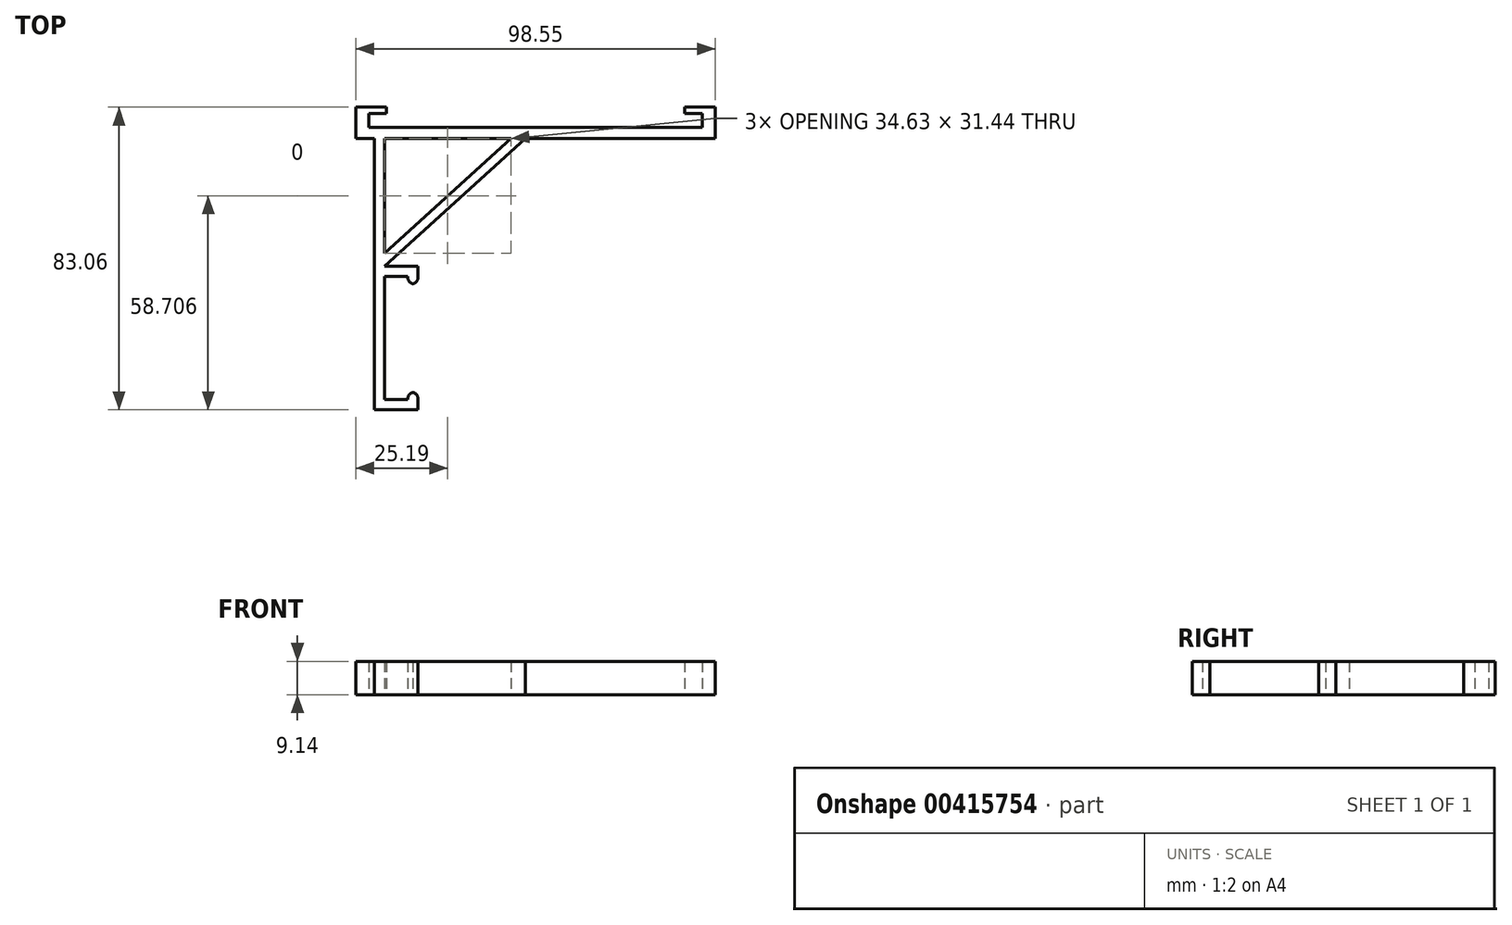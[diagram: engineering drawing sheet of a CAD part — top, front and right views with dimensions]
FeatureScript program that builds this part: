
annotation { "Feature Type Name" : "Feature", "Feature Type Description" : "" }
export const myFeature = defineFeature(function(context is Context, id is Id, definition is map)
    precondition{}
    {
        {
            var Q0;
            Q0=qCreatedBy(makeId("Top.planeOp"),FACE);
            var sketch = newSketch(context, id + "F0", { "sketchPlane" : qUnion([Q0])});
            skLineSegment(sketch, "E0", {"start": v(-45.89, 21.6) * mm, "end": v(-54.27, 21.6) * mm});
            skLineSegment(sketch, "E1", {"start": v(-54.27, 21.6) * mm, "end": v(-54.27, 12.96) * mm});
            skLineSegment(sketch, "E2", {"start": v(-54.27, 12.96) * mm, "end": v(-49.19, 12.96) * mm});
            skLineSegment(sketch, "E3", {"start": v(44.28, 12.96) * mm, "end": v(44.28, 21.6) * mm});
            skLineSegment(sketch, "E4", {"start": v(44.28, 21.6) * mm, "end": v(35.9, 21.6) * mm});
            skLineSegment(sketch, "E5", {"start": v(35.9, 21.6) * mm, "end": v(35.9, 19.81) * mm});
            skLineSegment(sketch, "E6", {"start": v(35.9, 19.81) * mm, "end": v(40.73, 19.81) * mm});
            skLineSegment(sketch, "E7", {"start": v(40.73, 19.81) * mm, "end": v(40.73, 16) * mm});
            skLineSegment(sketch, "E8", {"start": v(40.73, 16) * mm, "end": v(-50.71, 16) * mm});
            skLineSegment(sketch, "E9", {"start": v(-45.89, 21.6) * mm, "end": v(-45.89, 19.81) * mm});
            skLineSegment(sketch, "E10", {"start": v(-50.71, 16) * mm, "end": v(-50.71, 19.81) * mm});
            skLineSegment(sketch, "E11", {"start": v(-45.89, 19.81) * mm, "end": v(-50.71, 19.81) * mm});
            skLineSegment(sketch, "E12", {"start": v(-49.19, 12.96) * mm, "end": v(-49.19, -61.47) * mm});
            skLineSegment(sketch, "E13", {"start": v(-49.19, -61.47) * mm, "end": v(-37.25, -61.47) * mm});
            skLineSegment(sketch, "E14", {"start": v(-37.25, -61.47) * mm, "end": v(-37.25, -56.64) * mm});
            skLineSegment(sketch, "E15", {"start": v(-37.25, -56.64) * mm, "end": v(-40.04, -56.64) * mm});
            skLineSegment(sketch, "E16", {"start": v(-40.04, -56.64) * mm, "end": v(-40.04, -58.67) * mm});
            skLineSegment(sketch, "E17", {"start": v(-40.04, -58.67) * mm, "end": v(-46.4, -58.67) * mm});
            skLineSegment(sketch, "E18", {"start": v(-46.4, -58.67) * mm, "end": v(-46.4, -27.94) * mm});
            skLineSegment(sketch, "E19.trimOffspring", {"start": v(-46.4, -18.48) * mm, "end": v(-46.4, 12.96) * mm});
            skPoint(sketch, "E20.orphan", {"position": v(-40.04, -61.47) * mm});
            skLineSegment(sketch, "E21.trimOffspring", {"start": v(-46.4, 12.96) * mm, "end": v(-11.76, 12.96) * mm});
            skLineSegment(sketch, "E22.trimOffspring", {"start": v(-7.79, 12.96) * mm, "end": v(44.28, 12.96) * mm});
            skLineSegment(sketch, "E23", {"start": v(-46.4, -58.67) * mm, "end": v(-46.4, -37.38) * mm});
            skLineSegment(sketch, "E24", {"start": v(-46.4, -22.1) * mm, "end": v(-37.25, -22.1) * mm});
            skLineSegment(sketch, "E25", {"start": v(-37.25, -22.1) * mm, "end": v(-37.25, -26.92) * mm});
            skLineSegment(sketch, "E26", {"start": v(-37.25, -26.92) * mm, "end": v(-40.04, -26.92) * mm});
            skLineSegment(sketch, "E27", {"start": v(-40.04, -26.92) * mm, "end": v(-40.04, -24.89) * mm});
            skLineSegment(sketch, "E28", {"start": v(-40.04, -24.89) * mm, "end": v(-46.4, -24.89) * mm});
            skLineSegment(sketch, "E29", {"start": v(-46.4, -24.89) * mm, "end": v(-46.4, -27.94) * mm});
            skLineSegment(sketch, "E30", {"start": v(-7.79, 12.96) * mm, "end": v(-46.4, -22.1) * mm});
            skLineSegment(sketch, "E31", {"start": v(-11.76, 12.96) * mm, "end": v(-46.4, -18.48) * mm});
            skSolve(sketch);
        }
        {
            var Q0;
            Q0 = qSketchRegion(id + "F0", true);
            extrude(context, id + "F1", {"entities" : qUnion([Q0]), "depth" : 9.14 * mm});
        }
        {
            var Q0;
            Q0=makeQuery(id+"F1.opExtrude","SWEPT_EDGE",EDGE,{"disambiguationData":[OSD([sQuery(id+"F0.wireOp",EDGE,"E26"),sQuery(id+"F0.wireOp",EDGE,"E27")])]});
            var Q1;
            Q1=makeQuery(id+"F1.opExtrude","SWEPT_EDGE",EDGE,{"disambiguationData":[OSD([sQuery(id+"F0.wireOp",EDGE,"E25"),sQuery(id+"F0.wireOp",EDGE,"E26")])]});
            var Q2;
            Q2=makeQuery(id+"F1.opExtrude","SWEPT_EDGE",EDGE,{"disambiguationData":[OSD([sQuery(id+"F0.wireOp",EDGE,"E14"),sQuery(id+"F0.wireOp",EDGE,"E15")])]});
            var Q3;
            Q3=makeQuery(id+"F1.opExtrude","SWEPT_EDGE",EDGE,{"disambiguationData":[OSD([sQuery(id+"F0.wireOp",EDGE,"E15"),sQuery(id+"F0.wireOp",EDGE,"E16")])]});
            fillet(context, id + "F2", {"entities" : qUnion([Q0, Q1, Q2, Q3]), "radius" : 1.78 * mm, "tangentPropagation" : true, "allowEdgeOverflow" : false});
        }
    });
